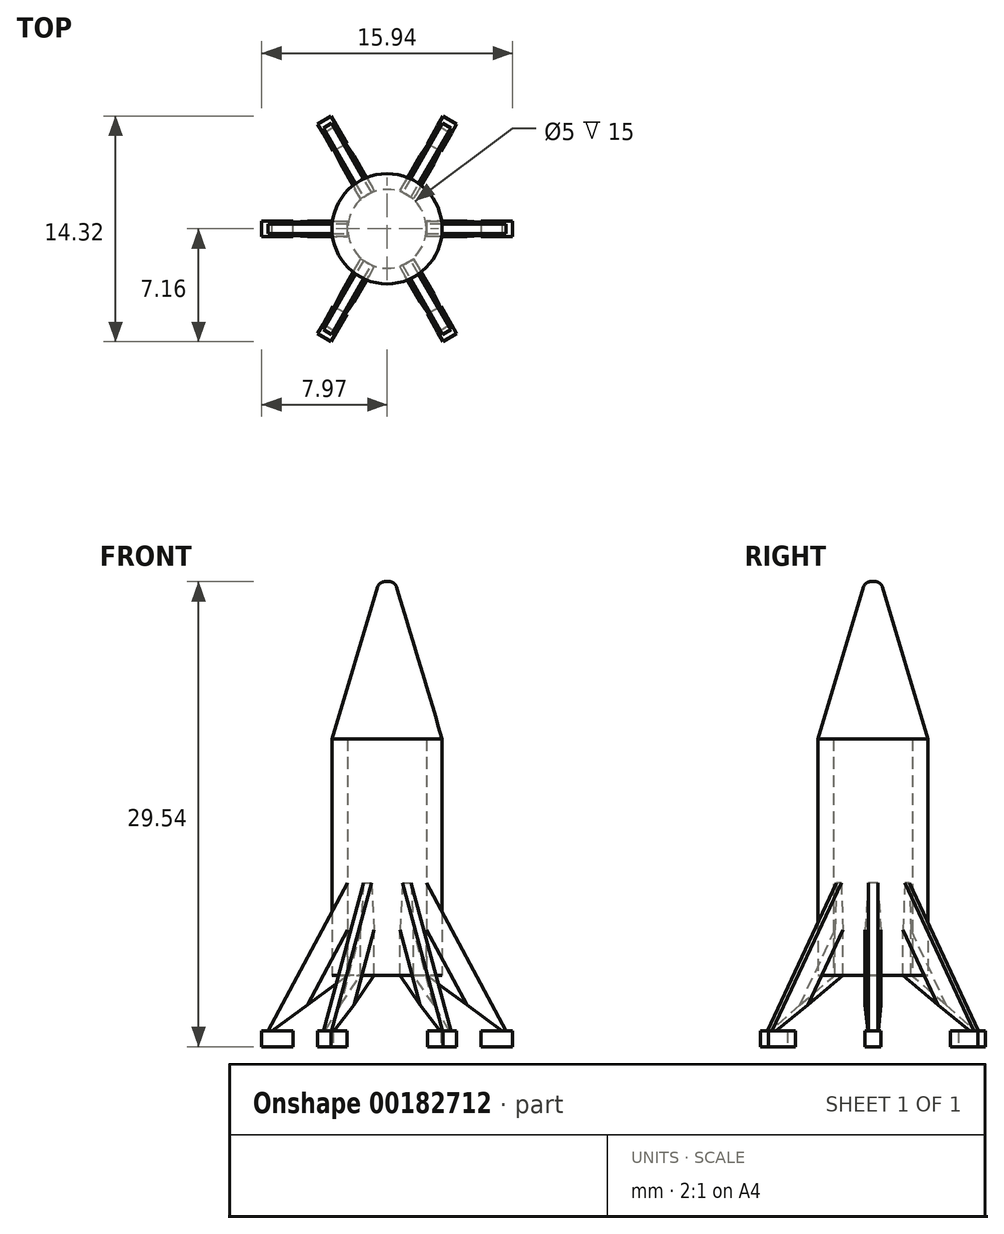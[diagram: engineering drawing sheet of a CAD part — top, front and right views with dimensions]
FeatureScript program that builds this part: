
annotation { "Feature Type Name" : "Feature", "Feature Type Description" : "" }
export const myFeature = defineFeature(function(context is Context, id is Id, definition is map)
    precondition{}
    {
        {
            var Q0;
            Q0=qCreatedBy(makeId("Top.planeOp"),FACE);
            var sketch = newSketch(context, id + "F0", { "sketchPlane" : qUnion([Q0])});
            skCircle(sketch, "E0", {"center": v(0, 0) * mm, "radius": 3.5 * mm});
            skCircle(sketch, "E1", {"center": v(0, 0) * mm, "radius": 2.5 * mm});
            skSolve(sketch);
        }
        {
            var Q0;
            Q0=makeQuery(id+"F0.imprint","IMPRINT",FACE,{"disambiguationData":[TD([[makeQuery(id+"F0.imprint","IMPRINT",EDGE,{"derivedFrom":sQuery(id+"F0.wireOp",EDGE,"E0")}),1.0]])]});
            var Q1;
            Q1 = qSketchRegion(id + "F2", true);
            extrude(context, id + "F1", {"entities" : qUnion([Q0, Q1]), "offsetDistance" : 25 * mm, "depth" : 15 * mm});
        }
        {
            var Q0;
            Q0=qCreatedBy(makeId("Front.planeOp"),FACE);
            var sketch = newSketch(context, id + "F2", { "sketchPlane" : qUnion([Q0])});
            skLineSegment(sketch, "E2.0", {"start": v(-3.5, 15) * mm, "end": v(3.5, 15) * mm});
            skLineSegment(sketch, "E3", {"start": v(-3.5, 15) * mm, "end": v(-0.5, 25) * mm});
            skLineSegment(sketch, "E4", {"start": v(0, 25) * mm, "end": v(0, 15) * mm});
            skLineSegment(sketch, "E5", {"start": v(-0.5, 25) * mm, "end": v(0, 25) * mm});
            skSolve(sketch);
        }
        {
            var Q0;
            {var subQ0=sQuery(id+"F2.wireOp",EDGE,"E3");Q0=makeQuery(id+"F2.imprint","IMPRINT",FACE,{"disambiguationData":[TD([[makeQuery(id+"F2.imprint","IMPRINT",EDGE,{"derivedFrom":subQ0}),-1.0]])]});}
            var Q1;
            Q1=sQuery(id+"F2.wireOp",EDGE,"E4");
            revolve(context, id + "F3", {"operationType" : NewBodyOperationType.ADD, "entities" : qUnion([Q0]), "axis" : qUnion([Q1]), "revolveType" : RevolveType.FULL});
        }
        {
            var Q0;
            Q0=qCreatedBy(makeId("Front.planeOp"),FACE);
            var sketch = newSketch(context, id + "F4", { "sketchPlane" : qUnion([Q0])});
            skLineSegment(sketch, "E6.0", {"start": v(-2.5, 0) * mm, "end": v(2.5, 0) * mm});
            skLineSegment(sketch, "E7", {"start": v(-2.5, 0) * mm, "end": v(-2.5, 5.88) * mm});
            skLineSegment(sketch, "E8", {"start": v(-2.5, 5.88) * mm, "end": v(-7.74, -3.87) * mm});
            skLineSegment(sketch, "E9", {"start": v(-7.74, -3.87) * mm, "end": v(-2.5, 0) * mm});
            skLineSegment(sketch, "E10.bottom", {"start": v(-7.97, -3.54) * mm, "end": v(-5.97, -3.54) * mm});
            skLineSegment(sketch, "E10.top", {"start": v(-7.97, -4.54) * mm, "end": v(-5.97, -4.54) * mm});
            skLineSegment(sketch, "E10.left", {"start": v(-7.97, -3.54) * mm, "end": v(-7.97, -4.54) * mm});
            skLineSegment(sketch, "E10.right", {"start": v(-5.97, -3.54) * mm, "end": v(-5.97, -4.54) * mm});
            skSolve(sketch);
        }
        {
            var Q0;
            Q0=makeQuery(id+"F4.imprint","IMPRINT",FACE,{"disambiguationData":[TD([[makeQuery(id+"F4.imprint","IMPRINT",EDGE,{"derivedFrom":sQuery(id+"F4.wireOp",EDGE,"E7")}),1.0]])]});
            var Q1;
            Q1=makeQuery(id+"F4.imprint","IMPRINT",FACE,{"disambiguationData":[TD([[makeQuery(id+"F4.imprint","IMPRINT",EDGE,{"derivedFrom":sQuery(id+"F4.wireOp",EDGE,"E10.top")}),1.0]])]});
            var Q2;
            {var subQ0=sQuery(id+"F4.wireOp",EDGE,"E9");var subQ1=sQuery(id+"F4.wireOp",EDGE,"E8");var subQ2=makeQuery(id+"F4.imprint","INTERSECT",VERTEX,{"derivedFrom":[subQ1,subQ0]});Q2=makeQuery(id+"F4.imprint","IMPRINT",FACE,{"disambiguationData":[TD([[makeQuery(id+"F4.imprint","IMPRINT",EDGE,{"disambiguationData":[TD([[subQ2,1.0]])],"derivedFrom":subQ1}),1.0]])]});}
            extrude(context, id + "F5", {"entities" : qUnion([Q0, Q1, Q2]), "endBound" : BoundingType.SYMMETRIC, "offsetDistance" : 25 * mm, "depth" : 1 * mm});
        }
        {
            var Q0;
            {var subQ0=sQuery(id+"F4.wireOp",EDGE,"E8");Q0=makeQuery(id+"F5.opExtrude","CAP_EDGE",EDGE,{"disambiguationData":[OSD([subQ0]),TDD([makeQuery(id+"F4.imprint","IMPRINT",EDGE,{"disambiguationData":[TD([[makeQuery(id+"F4.imprint","INTERSECT",VERTEX,{"derivedFrom":[sQuery(id+"F4.wireOp",EDGE,"E7"),subQ0]}),-1.0]])],"derivedFrom":subQ0})])],"isStart":false});}
            var Q1;
            {var subQ0=sQuery(id+"F4.wireOp",EDGE,"E8");Q1=makeQuery(id+"F5.opExtrude","CAP_EDGE",EDGE,{"disambiguationData":[OSD([subQ0]),TDD([makeQuery(id+"F4.imprint","IMPRINT",EDGE,{"disambiguationData":[TD([[makeQuery(id+"F4.imprint","INTERSECT",VERTEX,{"derivedFrom":[sQuery(id+"F4.wireOp",EDGE,"E7"),subQ0]}),-1.0]])],"derivedFrom":subQ0})])],"isStart":true});}
            chamfer(context, id + "F6", {"entities" : qUnion([Q0, Q1]), "chamferType" : ChamferType.OFFSET_ANGLE, "width" : 0.2 * mm, "oppositeDirection" : true, "angle" : 82 * degree});
        }
        {
            var Q0;
            Q0=makeQuery(id+"F5.opExtrude","SWEPT_BODY",BODY,{"disambiguationData":[OSD([sQuery(id+"F4.wireOp",EDGE,"E7"),sQuery(id+"F4.wireOp",EDGE,"E8"),sQuery(id+"F4.wireOp",EDGE,"E9")])]});
            var Q1;
            Q1=makeQuery(id+"F5.opExtrude","SWEPT_BODY",BODY,{"disambiguationData":[OSD([sQuery(id+"F4.wireOp",EDGE,"E10.bottom"),sQuery(id+"F4.wireOp",EDGE,"E10.top"),sQuery(id+"F4.wireOp",EDGE,"E10.left"),sQuery(id+"F4.wireOp",EDGE,"E10.right")])]});
            var Q2;
            Q2=sQuery(id+"F2.wireOp",EDGE,"E4");
            circularPattern(context, id + "F7", {"entities" : qUnion([Q0, Q1]), "axis" : qUnion([Q2]), "angle" : 60 * degree, "instanceCount" : 6});
        }
        {
            var Q0;
            Q0=makeQuery(id+"F3.opRevolve","SWEPT_EDGE",EDGE,{"disambiguationData":[OSD([sQuery(id+"F2.wireOp",EDGE,"E3"),sQuery(id+"F2.wireOp",EDGE,"E5")])]});
            fillet(context, id + "F8", {"entities" : qUnion([Q0]), "radius" : 0.5 * mm, "tangentPropagation" : true, "allowEdgeOverflow" : false});
        }
    });
